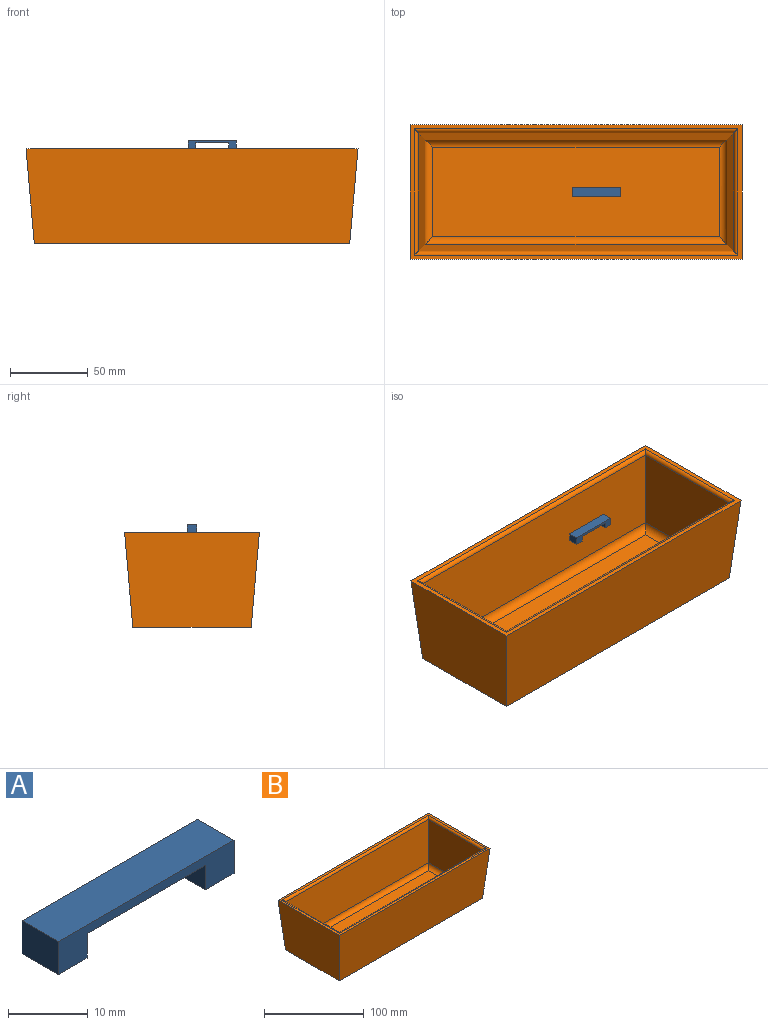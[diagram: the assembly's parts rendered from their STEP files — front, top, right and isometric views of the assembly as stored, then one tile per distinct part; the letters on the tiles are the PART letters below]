
ASSEMBLY  parts=2 mates=1
PART A: 10 faces, bbox 31.2x6.4x5.1 mm
  f0: plane 6.42x5.12mm, normal (0,0,-1), area 32.9mm2, adj f1,f2,f3,f9
  f1: plane 31.2x5.08mm, normal (0,-1,0), area 79.5mm2, adj f0,f2,f4,f5,f6,f7,f8,f9
  f2: plane 6.42x5.08mm, normal (1,0,0), area 32.6mm2, adj f0,f1,f3,f5
  f3: plane 31.2x5.08mm, normal (0,1,0), area 79.5mm2, adj f0,f2,f4,f5,f6,f7,f8,f9
  f4: plane 6.42x5.08mm, normal (-1,0,0), area 32.6mm2, adj f1,f3,f5,f6
  f5: plane 31.2x6.42mm, normal (0,0,1), area 200.4mm2, adj f1,f2,f3,f4
  f6: plane 6.42x5.12mm, normal (0,0,-1), area 32.9mm2, adj f1,f3,f4,f8
  f7: plane 20.97x6.42mm, normal (0,0,-1), area 134.7mm2, adj f1,f3,f8,f9
  f8: plane 6.42x3.77mm, normal (1,0,0), area 24.2mm2, adj f1,f3,f6,f7
  f9: plane 6.42x3.77mm, normal (-1,0,0), area 24.2mm2, adj f0,f1,f3,f7
PART B: 19 faces, bbox 213.9x86.9x61 mm
  f0: plane 213.87x86.87mm, normal (0,0,1), area 1636.5mm2, adj f1,f2,f3,f4,f11,f12,f13,f14
  f1: plane 213.87x60.96mm, normal (0,-1,-0.09), area 12760.7mm2, adj f0,f2,f4,f5
  f2: plane 86.87x60.96mm, normal (1,0,-0.09), area 4989.3mm2, adj f0,f1,f3,f5
  f3: plane 213.87x60.96mm, normal (0,1,-0.09), area 12760.7mm2, adj f0,f2,f4,f5
  f4: plane 86.87x60.96mm, normal (-1,0,-0.09), area 4989.3mm2, adj f0,f1,f3,f5
  f5: plane 203.2x76.2mm, normal (0,0,-1), area 15483.8mm2, adj f1,f2,f3,f4
  f6: plane 203.26x48.92mm, normal (0,1,0.09), area 9772.2mm2, adj f7,f9,f13,f17
  f7: plane 76.26x48.92mm, normal (-1,0,0.09), area 3535.1mm2, adj f6,f8,f11,f15
  f8: plane 203.26x48.92mm, normal (0,-1,0.09), area 9772.2mm2, adj f7,f9,f12,f16
  f9: plane 76.26x48.92mm, normal (1,0,0.09), area 3535.1mm2, adj f6,f8,f14,f18
  f10: plane 184.58x57.58mm, normal (0,0,1), area 10628.2mm2, adj f15,f16,f17,f18
  f11: cylinder r=2.54mm len=81.32mm, axis (0,1,0), area 294.7mm2, adj f0,f7,f12,f13
  f12: cylinder r=2.54mm len=208.32mm, axis (1,0,0), area 773.2mm2, adj f0,f8,f11,f14
  f13: cylinder r=2.54mm len=208.32mm, axis (1,0,0), area 773.2mm2, adj f0,f6,f11,f14
  f14: cylinder r=2.54mm len=81.32mm, axis (0,1,0), area 294.7mm2, adj f0,f9,f12,f13
  f15: cylinder r=5.08mm len=67.7mm, axis (0,-1,0), area 481.1mm2, adj f7,f10,f16,f17
  f16: cylinder r=5.08mm len=194.7mm, axis (-1,0,0), area 1438.2mm2, adj f8,f10,f15,f18
  f17: cylinder r=5.08mm len=194.7mm, axis (-1,0,0), area 1438.2mm2, adj f6,f10,f15,f18
  f18: cylinder r=5.08mm len=67.7mm, axis (0,-1,0), area 481.1mm2, adj f9,f10,f16,f17
PLACE A t=(-71.17,-74.57,18.05)mm
PLACE B t=(-84.21,-74.57,-42.91)mm fixed
MATE fastened B.f0 <-> A.f6  axis (0,0,1) through (-84.21,-74.57,18.05)mm
